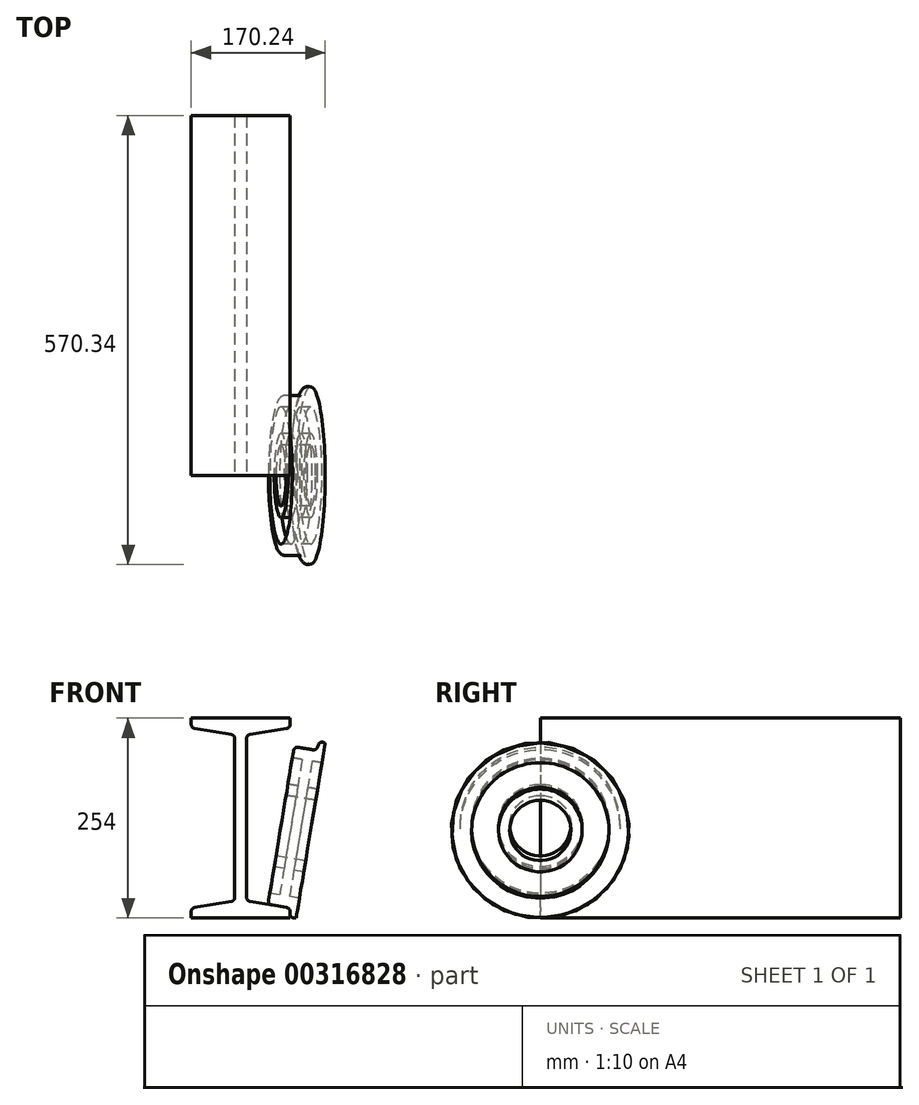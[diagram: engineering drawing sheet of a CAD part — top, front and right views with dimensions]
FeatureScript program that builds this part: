
annotation { "Feature Type Name" : "Feature", "Feature Type Description" : "" }
export const myFeature = defineFeature(function(context is Context, id is Id, definition is map)
    precondition{}
    {
        {
            var Q0;
            Q0=qCreatedBy(makeId("Front.planeOp"),FACE);
            var sketch = newSketch(context, id + "F0", { "sketchPlane" : qUnion([Q0])});
            skLineSegment(sketch, "E0.left", {"start": v(7.54, 105.32) * mm, "end": v(7.54, -105.32) * mm});
            skLineSegment(sketch, "E0.right", {"start": v(-7.54, 105.32) * mm, "end": v(-7.54, -105.32) * mm});
            skPoint(sketch, "E0.middle", {"position": v(0, 0) * mm});
            skPoint(sketch, "E1.endSnap0", {"position": v(0, 120.76) * mm});
            skLineSegment(sketch, "E2.top", {"start": v(62.79, 127) * mm, "end": v(-62.79, 127) * mm});
            skLineSegment(sketch, "E2.left", {"start": v(62.79, 114.53) * mm, "end": v(62.79, 127) * mm});
            skLineSegment(sketch, "E2.right", {"start": v(-62.79, 114.53) * mm, "end": v(-62.79, 127) * mm});
            skPoint(sketch, "E0.bottom.end.orphan", {"position": v(-7.54, 120.76) * mm});
            skLineSegment(sketch, "E3.bottom", {"start": v(62.79, -127) * mm, "end": v(-62.79, -127) * mm});
            skLineSegment(sketch, "E3.left", {"start": v(62.79, -127) * mm, "end": v(62.79, -114.53) * mm});
            skLineSegment(sketch, "E3.right", {"start": v(-62.79, -127) * mm, "end": v(-62.79, -114.53) * mm});
            skLineSegment(sketch, "E4.trimOffspring", {"start": v(-47.55, -114.53) * mm, "end": v(-62.79, -114.53) * mm});
            skLineSegment(sketch, "E5", {"start": v(0, 0) * mm, "end": v(0, -152.67) * mm, "construction": true});
            skLineSegment(sketch, "E6", {"start": v(62.79, -114.53) * mm, "end": v(7.54, -105.32) * mm});
            skLineSegment(sketch, "E7", {"start": v(-47.55, -114.53) * mm, "end": v(-47.55, -111.99) * mm});
            skLineSegment(sketch, "E8", {"start": v(-62.79, -114.53) * mm, "end": v(-7.54, -105.32) * mm});
            skLineSegment(sketch, "E9", {"start": v(-62.79, 114.53) * mm, "end": v(-47.55, 114.53) * mm});
            skLineSegment(sketch, "E10", {"start": v(-47.55, 114.53) * mm, "end": v(-47.55, 111.99) * mm});
            skLineSegment(sketch, "E11", {"start": v(62.79, 114.53) * mm, "end": v(47.55, 114.53) * mm});
            skLineSegment(sketch, "E12", {"start": v(47.55, 114.53) * mm, "end": v(47.55, 111.99) * mm});
            skLineSegment(sketch, "E13", {"start": v(-62.79, 114.53) * mm, "end": v(-7.54, 105.32) * mm});
            skLineSegment(sketch, "E14", {"start": v(62.79, 114.53) * mm, "end": v(7.54, 105.32) * mm});
            skPoint(sketch, "E15.orphan", {"position": v(0, 187.21) * mm});
            skPoint(sketch, "E16.orphan", {"position": v(7.54, 120.76) * mm});
            skLineSegment(sketch, "E17", {"start": v(59.65, -114.53) * mm, "end": v(59.74, -114.02) * mm});
            skLineSegment(sketch, "E18", {"start": v(59.74, -114.02) * mm, "end": v(59.65, -114.53) * mm});
            skSolve(sketch);
        }
        {
            var Q0;
            Q0 = qSketchRegion(id + "F0", true);
            extrude(context, id + "F1", {"entities" : qUnion([Q0]), "oppositeDirection" : true, "depth" : 457.2 * mm});
        }
        {
            var Q0;
            Q0=makeQuery(id+"F1.opExtrude","SWEPT_EDGE",EDGE,{"disambiguationData":[OSD([sQuery(id+"F0.wireOp",EDGE,"E0.left"),sQuery(id+"F0.wireOp",EDGE,"E6")])]});
            var Q1;
            Q1=makeQuery(id+"F1.opExtrude","SWEPT_EDGE",EDGE,{"disambiguationData":[OSD([sQuery(id+"F0.wireOp",EDGE,"E0.right"),sQuery(id+"F0.wireOp",EDGE,"E8")])]});
            var Q2;
            Q2=makeQuery(id+"F1.opExtrude","SWEPT_EDGE",EDGE,{"disambiguationData":[OSD([sQuery(id+"F0.wireOp",EDGE,"E0.right"),sQuery(id+"F0.wireOp",EDGE,"E13")])]});
            var Q3;
            Q3=makeQuery(id+"F1.opExtrude","SWEPT_EDGE",EDGE,{"disambiguationData":[OSD([sQuery(id+"F0.wireOp",EDGE,"E0.left"),sQuery(id+"F0.wireOp",EDGE,"E14")])]});
            var Q4;
            Q4=makeQuery(id+"F1.opExtrude","SWEPT_EDGE",EDGE,{"disambiguationData":[OSD([sQuery(id+"F0.wireOp",EDGE,"TwWKh1By-0Wmj-WCUU-F3rA-mpvFiguGvyDf"),sQuery(id+"F0.wireOp",EDGE,"E6"),sQuery(id+"F0.wireOp",EDGE,"E3.left")])]});
            var Q5;
            Q5=makeQuery(id+"F1.opExtrude","SWEPT_EDGE",EDGE,{"disambiguationData":[OSD([sQuery(id+"F0.wireOp",EDGE,"E3.right"),sQuery(id+"F0.wireOp",EDGE,"E4.trimOffspring"),sQuery(id+"F0.wireOp",EDGE,"E8")])]});
            var Q6;
            Q6=makeQuery(id+"F1.opExtrude","SWEPT_EDGE",EDGE,{"disambiguationData":[OSD([sQuery(id+"F0.wireOp",EDGE,"E2.right"),sQuery(id+"F0.wireOp",EDGE,"E9"),sQuery(id+"F0.wireOp",EDGE,"E13")])]});
            var Q7;
            Q7=makeQuery(id+"F1.opExtrude","SWEPT_EDGE",EDGE,{"disambiguationData":[OSD([sQuery(id+"F0.wireOp",EDGE,"E2.left"),sQuery(id+"F0.wireOp",EDGE,"E11"),sQuery(id+"F0.wireOp",EDGE,"E14")])]});
            fillet(context, id + "F2", {"entities" : qUnion([Q0, Q1, Q2, Q3, Q4, Q5, Q6, Q7]), "radius" : 5.08 * mm, "tangentPropagation" : true, "allowEdgeOverflow" : false});
        }
        {
            var Q0;
            Q0=makeQuery(id+"F1.opExtrude","CAP_FACE",FACE,{"disambiguationData":[OSD([sQuery(id+"F0.wireOp",EDGE,"E0.left"),sQuery(id+"F0.wireOp",EDGE,"E0.right"),sQuery(id+"F0.wireOp",EDGE,"E2.top"),sQuery(id+"F0.wireOp",EDGE,"E2.left"),sQuery(id+"F0.wireOp",EDGE,"E2.right"),sQuery(id+"F0.wireOp",EDGE,"E3.bottom"),sQuery(id+"F0.wireOp",EDGE,"E3.right"),sQuery(id+"F0.wireOp",EDGE,"E6"),sQuery(id+"F0.wireOp",EDGE,"E8"),sQuery(id+"F0.wireOp",EDGE,"E13"),sQuery(id+"F0.wireOp",EDGE,"E14"),sQuery(id+"F0.wireOp",EDGE,"E3.left")])],"isStart":true});
            var sketch = newSketch(context, id + "F3", { "sketchPlane" : qUnion([Q0])});
            skLineSegment(sketch, "E19", {"start": v(58.54, -113.82) * mm, "end": v(34.64, -109.84) * mm});
            skArc(sketch, "E20", {"start": v(62.79, -118.83) * mm, "mid": v(61.58, -115.55) * mm, "end": v(58.54, -113.82) * mm});
            skLineSegment(sketch, "E21", {"start": v(62.79, -127) * mm, "end": v(62.79, -118.83) * mm});
            skLineSegment(sketch, "E22", {"start": v(62.79, -127) * mm, "end": v(70.4, -127) * mm});
            skLineSegment(sketch, "E23", {"start": v(70.4, -127) * mm, "end": v(74.58, -101.95) * mm});
            skLineSegment(sketch, "E24", {"start": v(37, -95.68) * mm, "end": v(34.64, -109.84) * mm});
            skLineSegment(sketch, "E25", {"start": v(40.32, -7.78) * mm, "end": v(83.67, -15) * mm, "construction": true});
            skLineSegment(sketch, "E26", {"start": v(42.6, -62.13) * mm, "end": v(44.95, -47.97) * mm});
            skLineSegment(sketch, "E27", {"start": v(44.95, -47.97) * mm, "end": v(82.54, -54.24) * mm});
            skLineSegment(sketch, "E28.MirrorCS", {"start": v(80.18, -68.4) * mm, "end": v(82.54, -54.24) * mm});
            skLineSegment(sketch, "E29", {"start": v(42.6, -62.13) * mm, "end": v(55.12, -64.22) * mm});
            skLineSegment(sketch, "E30", {"start": v(67.65, -66.3) * mm, "end": v(80.18, -68.4) * mm});
            skLineSegment(sketch, "E31.0", {"start": v(62.06, -99.86) * mm, "end": v(67.65, -66.3) * mm});
            skLineSegment(sketch, "E32.0", {"start": v(49.53, -97.77) * mm, "end": v(55.12, -64.22) * mm});
            skLineSegment(sketch, "E33", {"start": v(49.53, -97.77) * mm, "end": v(37, -95.68) * mm});
            skLineSegment(sketch, "E34", {"start": v(62.06, -99.86) * mm, "end": v(74.58, -101.95) * mm});
            skSolve(sketch);
        }
        {
            var Q0;
            Q0=makeQuery(id+"F3.imprint","IMPRINT",FACE,{"disambiguationData":[TD([[makeQuery(id+"F3.imprint","IMPRINT",EDGE,{"derivedFrom":sQuery(id+"F3.wireOp",EDGE,"E19")}),-1.0]])]});
            var Q1;
            Q1=sQuery(id+"F3.wireOp",EDGE,"E25");
            revolve(context, id + "F4", {"entities" : qUnion([Q0]), "axis" : qUnion([Q1]), "revolveType" : RevolveType.FULL});
        }
        {
            var Q0;
            Q0=makeQuery(id+"F4.opRevolve","SWEPT_EDGE",EDGE,{"disambiguationData":[OSD([sQuery(id+"F0.wireOp",EDGE,"E6"),sQuery(id+"F3.wireOp",EDGE,"E19"),sQuery(id+"F3.wireOp",EDGE,"E24")])]});
            var Q1;
            Q1=makeQuery(id+"F4.opRevolve","SWEPT_FACE",FACE,{"disambiguationData":[OSD([sQuery(id+"F3.wireOp",EDGE,"E21")])]});
            fillet(context, id + "F5", {"entities" : qUnion([Q0, Q1]), "radius" : 5.08 * mm, "tangentPropagation" : true, "allowEdgeOverflow" : false});
        }
    });
